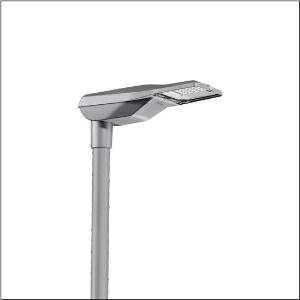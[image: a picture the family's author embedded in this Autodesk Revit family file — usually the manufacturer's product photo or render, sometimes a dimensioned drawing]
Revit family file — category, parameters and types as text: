
# Revit family: streetlight_sl_21_iq_micro___st1_5a_5xe1p41d08cb_4bae
name_source: partatom
category: Lighting Fixtures
units: mm (PartAtom-declared; Revit-internal decimal feet)

## family parameters
Cut with Voids When Loaded = No
Host = Face
Light Source = No
Part Type = Normal
Room Calculation Point = No
Round Connector Dimension = Use Diameter
Shared = No

## types (1)
- --- (1 x LED, 2930 lm, 19.4 W, 4000K)
    Apparent Load = 19 VA
    CIE Flux Codes = 22 53 95 100 100
    Color Rendering = 70
    Color Temperature = 4000K
    Default Elevation = 1800 mm
    Description = Streetlight SL 21 iQ micro, mast luminaire, primary light control with lens, of PMMA, primary optical cover: cover, of toughened safety glass, transparent, light distribution: ST1.5a, light emission: direct distribution, primary light characteristic: asymmetric, installation type: post-top, side-entry, LED, High Power LED, rated luminous flux: 2.930lm, luminous efficacy: 151lm/W, light colour: 740, colour temperature: 4000K, control: Auto-Match, Temp-Guard, Lumen-Switch, Night-Set, Smart-Wire, Light-Fading, Desk-Remote (wireless, voltage-free reading and setting of iQ features in the workshop via application-optimized NFC function/RFID function), optimised constant luminous flux control (CLO 2.0), presetting dimming linear, mains connection: 220..240V, AC, 50/60Hz, start of lifetime: 19W, end of service life: 20W, reduction: 10W, luminaire housing, of diecast aluminium, powder-coated, Siteco® metallic grey (DB 702S), corrosivity category C5 mid according to DIN EN ISO 12944, please order mast flange separately, inclination adjustable: 0°, 5°, 10°, 15°, sealing non-destructively replaceable, multi-level sealing system, length: 528mm, width: 235mm, height: 110mm, mast flange for spigot size: 42mm (side-entry): 5XC10008XM4, 60/48mm (side-entry/post-top): 5XC10108XM2, 76/60mm (side-entry/post-top): 5XC10108XM1, protection rating (complete): IP66, insulation class (complete): insulation class II (safety insulation), certification: CE, ENEC, ENEC+, VDE, impact resistance: IK09, permissible operating ambient temperature for outdoor applications: -40..+50°C, standard-compliant lighting for roads and squares, packaging unit: 1 piece

Light Distribution: ST1.5a
    Height = 110 mm
    Lamp = 1 x LED
    Lamp Light Flux = 2930 lm
    Lamp Power = 19.4 W
    Lamp count = 1
    Length = 528 mm
    Luminous efficacy = 151 lm/W
    Manufacturer = Siteco
    ModVariant = No
    Model = 5XE1P41D08CB
    Number of Poles = 1
    OnlyDefault = Yes
    Power Factor = 1
    Product Name = Streetlight SL 21 iQ micro | ST1.5a
    Product group = mast luminaire | pylon top
    ProductGroupID = 6100
    Protection Class = Protection class II
    Protection Degree = IP 66
    RLX_Detail_Level = 1
    RLX_Emergency_Light_Flux = 0 lm
    RLX_Emergency_Type = 0
    RLX_Emergency_Type_DB = No
    RlxData = <blob elided: 102533 chars, md5=a9cf8861>
    Socket = socket
    Standby Power = 0 W
    System Light Flux = 2930 lm
    System Power = 19 W
    Type Comments = factory setting: luminous flux: 100 % | dim-lin: 254 | 387 mA
    Type Image = l_1006881.jpg
    URL = http://relux.com
    VarID = @adj_069361
    Voltage = 0 V
    Weight = 0.00 kg
    Width = 235 mm

## geometry (parser evidence)
native form markers: Blend x4, Sweep x8
no freeform markers — native parametric forms only
